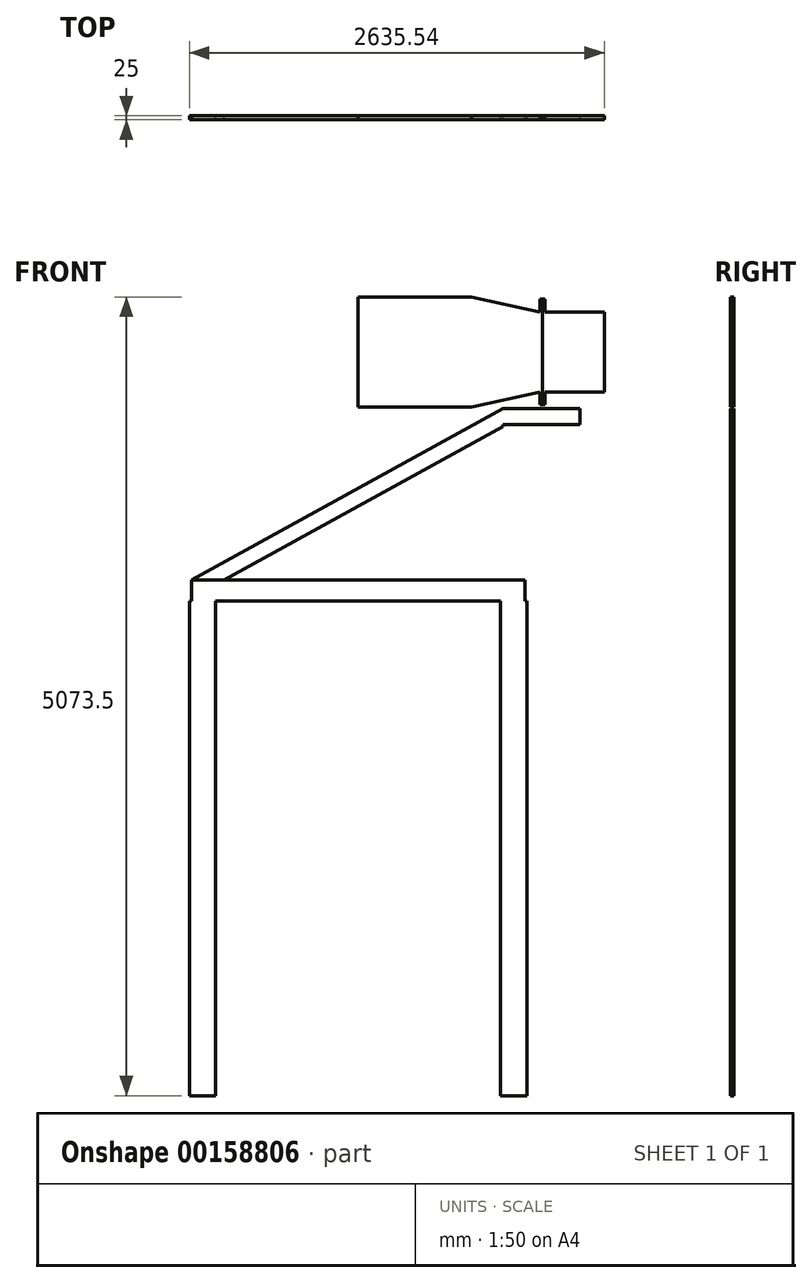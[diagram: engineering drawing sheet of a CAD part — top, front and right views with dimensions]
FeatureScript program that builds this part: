
annotation { "Feature Type Name" : "Feature", "Feature Type Description" : "" }
export const myFeature = defineFeature(function(context is Context, id is Id, definition is map)
    precondition{}
    {
        {
            var Q0;
            Q0=qCreatedBy(makeId("Front.planeOp"),FACE);
            var sketch = newSketch(context, id + "F0", { "sketchPlane" : qUnion([Q0])});
            skLineSegment(sketch, "E0", {"start": v(0, 0) * mm, "end": v(0, 3142.5) * mm});
            skLineSegment(sketch, "E1", {"start": v(0, 3142.5) * mm, "end": v(-168.3, 3142.5) * mm});
            skLineSegment(sketch, "E2", {"start": v(-168.3, 3142.5) * mm, "end": v(-168.3, 0) * mm});
            skLineSegment(sketch, "E3", {"start": v(-168.3, 0) * mm, "end": v(0, 0) * mm});
            skLineSegment(sketch, "E4", {"start": v(-14.15, 3275.5) * mm, "end": v(-14.15, 3142.5) * mm});
            skLineSegment(sketch, "E5", {"start": v(-14.15, 3142.5) * mm, "end": v(-2131.85, 3142.5) * mm});
            skLineSegment(sketch, "E6", {"start": v(-2131.85, 3142.5) * mm, "end": v(-2131.85, 3275.5) * mm});
            skLineSegment(sketch, "E7", {"start": v(-2131.85, 3275.5) * mm, "end": v(-14.15, 3275.5) * mm});
            skLineSegment(sketch, "E8", {"start": v(489.54, 4977.5) * mm, "end": v(489.54, 4469.5) * mm});
            skLineSegment(sketch, "E9", {"start": v(489.54, 4469.5) * mm, "end": v(112, 4469.5) * mm});
            skLineSegment(sketch, "E10", {"start": v(112, 4469.5) * mm, "end": v(112, 4977.5) * mm});
            skLineSegment(sketch, "E11", {"start": v(112, 4977.5) * mm, "end": v(489.54, 4977.5) * mm});
            skLineSegment(sketch, "E12", {"start": v(112, 4977.5) * mm, "end": v(112, 5058.5) * mm});
            skLineSegment(sketch, "E13", {"start": v(112, 5058.5) * mm, "end": v(97, 5058.5) * mm});
            skLineSegment(sketch, "E14", {"start": v(97, 5058.5) * mm, "end": v(97, 4388.5) * mm});
            skLineSegment(sketch, "E15", {"start": v(97, 4388.5) * mm, "end": v(112, 4388.5) * mm});
            skLineSegment(sketch, "E16", {"start": v(112, 4388.5) * mm, "end": v(112, 4469.5) * mm});
            skLineSegment(sketch, "E17", {"start": v(489.54, 4723.5) * mm, "end": v(-1595.34, 4723.5) * mm, "construction": true});
            skLineSegment(sketch, "E18", {"start": v(-84.15, 3142.5) * mm, "end": v(-84.15, 3949.04) * mm, "construction": true});
            skLineSegment(sketch, "E19", {"start": v(-1073, 3142.5) * mm, "end": v(-1073, 5790.92) * mm, "construction": true});
            skLineSegment(sketch, "E20.MirrorCS", {"start": v(-1977.7, 3142.5) * mm, "end": v(-1977.7, 0) * mm});
            skLineSegment(sketch, "E21.MirrorCS", {"start": v(-2146, 0) * mm, "end": v(-2146, 3142.5) * mm});
            skLineSegment(sketch, "E22.MirrorCS", {"start": v(-1977.7, 0) * mm, "end": v(-2146, 0) * mm});
            skLineSegment(sketch, "E23", {"start": v(-154.15, 3275.5) * mm, "end": v(-154.15, 3142.5) * mm});
            skLineSegment(sketch, "E24.MirrorCS", {"start": v(-1991.85, 3275.5) * mm, "end": v(-1991.85, 3142.5) * mm});
            skLineSegment(sketch, "E25.bottom", {"start": v(97, 5058.5) * mm, "end": v(82, 5058.5) * mm});
            skLineSegment(sketch, "E25.top", {"start": v(97, 4388.5) * mm, "end": v(82, 4388.5) * mm});
            skLineSegment(sketch, "E25.right", {"start": v(82, 5058.5) * mm, "end": v(82, 4388.5) * mm});
            skLineSegment(sketch, "E26.bottom", {"start": v(-1073, 5073.5) * mm, "end": v(-353, 5073.5) * mm});
            skLineSegment(sketch, "E26.top", {"start": v(-1073, 4373.5) * mm, "end": v(-353, 4373.5) * mm});
            skLineSegment(sketch, "E26.left", {"start": v(-1073, 5073.5) * mm, "end": v(-1073, 4373.5) * mm});
            skLineSegment(sketch, "E26.right", {"start": v(-353, 5073.5) * mm, "end": v(-353, 4373.5) * mm});
            skLineSegment(sketch, "E27", {"start": v(-353, 5073.5) * mm, "end": v(82, 4977.5) * mm});
            skLineSegment(sketch, "E28", {"start": v(82, 4469.5) * mm, "end": v(-353, 4373.5) * mm});
            skLineSegment(sketch, "E29", {"start": v(-2131.85, 3142.5) * mm, "end": v(-2146, 3142.5) * mm});
            skLineSegment(sketch, "E30.bottom", {"start": v(-14.15, 3275.5) * mm, "end": v(-154.15, 3275.5) * mm});
            skLineSegment(sketch, "E30.top", {"start": v(-14.15, 4263.18) * mm, "end": v(-154.15, 4263.18) * mm});
            skLineSegment(sketch, "E30.left", {"start": v(-14.15, 3275.5) * mm, "end": v(-14.15, 4263.18) * mm});
            skLineSegment(sketch, "E30.right", {"start": v(-154.15, 3275.5) * mm, "end": v(-154.15, 4263.18) * mm});
            skLineSegment(sketch, "E31.bottom", {"start": v(-154.15, 4263.18) * mm, "end": v(336.6, 4263.18) * mm});
            skLineSegment(sketch, "E31.top", {"start": v(-154.15, 4363.18) * mm, "end": v(336.6, 4363.18) * mm});
            skLineSegment(sketch, "E31.left", {"start": v(-154.15, 4263.18) * mm, "end": v(-154.15, 4363.18) * mm});
            skLineSegment(sketch, "E31.right", {"start": v(336.6, 4263.18) * mm, "end": v(336.6, 4363.18) * mm});
            skLineSegment(sketch, "E32.bottom", {"start": v(336.6, 4469.5) * mm, "end": v(236.6, 4469.5) * mm});
            skLineSegment(sketch, "E32.top", {"start": v(336.6, 4363.18) * mm, "end": v(236.6, 4363.18) * mm});
            skLineSegment(sketch, "E32.left", {"start": v(336.6, 4469.5) * mm, "end": v(336.6, 4363.18) * mm});
            skLineSegment(sketch, "E32.right", {"start": v(236.6, 4469.5) * mm, "end": v(236.6, 4363.18) * mm});
            skLineSegment(sketch, "E33", {"start": v(-154.15, 4363.18) * mm, "end": v(-2131.85, 3275.5) * mm});
            skLineSegment(sketch, "E34", {"start": v(-1924.34, 3275.5) * mm, "end": v(-154.15, 4249.05) * mm});
            skSolve(sketch);
        }
        {
            var Q0;
            Q0=makeQuery(id+"F0.imprint","IMPRINT",FACE,{"disambiguationData":[TD([[makeQuery(id+"F0.imprint","IMPRINT",EDGE,{"derivedFrom":sQuery(id+"F0.wireOp",EDGE,"E0")}),1.0]])]});
            var Q1;
            {var subQ0=sQuery(id+"F0.wireOp",EDGE,"E20.MirrorCS");Q1=makeQuery(id+"F0.imprint","IMPRINT",FACE,{"disambiguationData":[TD([[makeQuery(id+"F0.imprint","IMPRINT",EDGE,{"derivedFrom":subQ0}),-1.0]])]});}
            var Q2;
            {var subQ0=sQuery(id+"F0.wireOp",EDGE,"E6");Q2=makeQuery(id+"F0.imprint","IMPRINT",FACE,{"disambiguationData":[TD([[makeQuery(id+"F0.imprint","IMPRINT",EDGE,{"derivedFrom":subQ0}),-1.0]])]});}
            var Q3;
            {var subQ6=sQuery(id+"F0.wireOp",EDGE,"E23");Q3=makeQuery(id+"F0.imprint","IMPRINT",FACE,{"disambiguationData":[TD([[makeQuery(id+"F0.imprint","IMPRINT",EDGE,{"derivedFrom":subQ6}),-1.0]])]});}
            var Q4;
            {var subQ0=sQuery(id+"F0.wireOp",EDGE,"E4");Q4=makeQuery(id+"F0.imprint","IMPRINT",FACE,{"disambiguationData":[TD([[makeQuery(id+"F0.imprint","IMPRINT",EDGE,{"derivedFrom":subQ0}),-1.0]])]});}
            extrude(context, id + "F1", {"entities" : qUnion([Q0, Q1, Q2, Q3, Q4]), "depth" : 25 * mm});
        }
        {
            var Q0;
            {var subQ4=sQuery(id+"F0.wireOp",EDGE,"E30.bottom");Q0=makeQuery(id+"F0.imprint","IMPRINT",FACE,{"disambiguationData":[TD([[makeQuery(id+"F0.imprint","IMPRINT",EDGE,{"derivedFrom":subQ4}),-1.0]])]});}
            var Q1;
            {var subQ0=sQuery(id+"F0.wireOp",EDGE,"E31.left");Q1=makeQuery(id+"F0.imprint","IMPRINT",FACE,{"disambiguationData":[TD([[makeQuery(id+"F0.imprint","IMPRINT",EDGE,{"derivedFrom":subQ0}),1.0]])]});}
            var Q2;
            Q2=makeQuery(id+"F0.imprint","IMPRINT",FACE,{"disambiguationData":[TD([[makeQuery(id+"F0.imprint","IMPRINT",EDGE,{"derivedFrom":sQuery(id+"F0.wireOp",EDGE,"E31.top")}),-1.0]])]});
            var Q3;
            Q3=makeQuery(id+"F0.imprint","IMPRINT",FACE,{"disambiguationData":[TD([[makeQuery(id+"F0.imprint","IMPRINT",EDGE,{"derivedFrom":sQuery(id+"F0.wireOp",EDGE,"E32.bottom")}),1.0]])]});
            extrude(context, id + "F2", {"entities" : qUnion([Q0, Q1, Q2, Q3]), "depth" : 25 * mm});
        }
        {
            var Q0;
            Q0=makeQuery(id+"F0.imprint","IMPRINT",FACE,{"disambiguationData":[TD([[makeQuery(id+"F0.imprint","IMPRINT",EDGE,{"derivedFrom":sQuery(id+"F0.wireOp",EDGE,"E26.bottom")}),-1.0]])]});
            var Q1;
            Q1=makeQuery(id+"F0.imprint","IMPRINT",FACE,{"disambiguationData":[TD([[makeQuery(id+"F0.imprint","IMPRINT",EDGE,{"derivedFrom":sQuery(id+"F0.wireOp",EDGE,"E26.right")}),1.0]])]});
            var Q2;
            {var subQ1=sQuery(id+"F0.wireOp",EDGE,"E25.bottom");Q2=makeQuery(id+"F0.imprint","IMPRINT",FACE,{"disambiguationData":[TD([[makeQuery(id+"F0.imprint","IMPRINT",EDGE,{"derivedFrom":subQ1}),1.0]])]});}
            extrude(context, id + "F3", {"entities" : qUnion([Q0, Q1, Q2]), "depth" : 25 * mm});
        }
        {
            var Q0;
            Q0=makeQuery(id+"F0.imprint","IMPRINT",FACE,{"disambiguationData":[TD([[makeQuery(id+"F0.imprint","IMPRINT",EDGE,{"derivedFrom":sQuery(id+"F0.wireOp",EDGE,"E10")}),1.0]])]});
            var Q1;
            {var subQ3=sQuery(id+"F0.wireOp",EDGE,"E8");Q1=makeQuery(id+"F0.imprint","IMPRINT",FACE,{"disambiguationData":[TD([[makeQuery(id+"F0.imprint","IMPRINT",EDGE,{"derivedFrom":subQ3}),-1.0]])]});}
            extrude(context, id + "F4", {"entities" : qUnion([Q0, Q1]), "depth" : 25 * mm});
        }
    });
